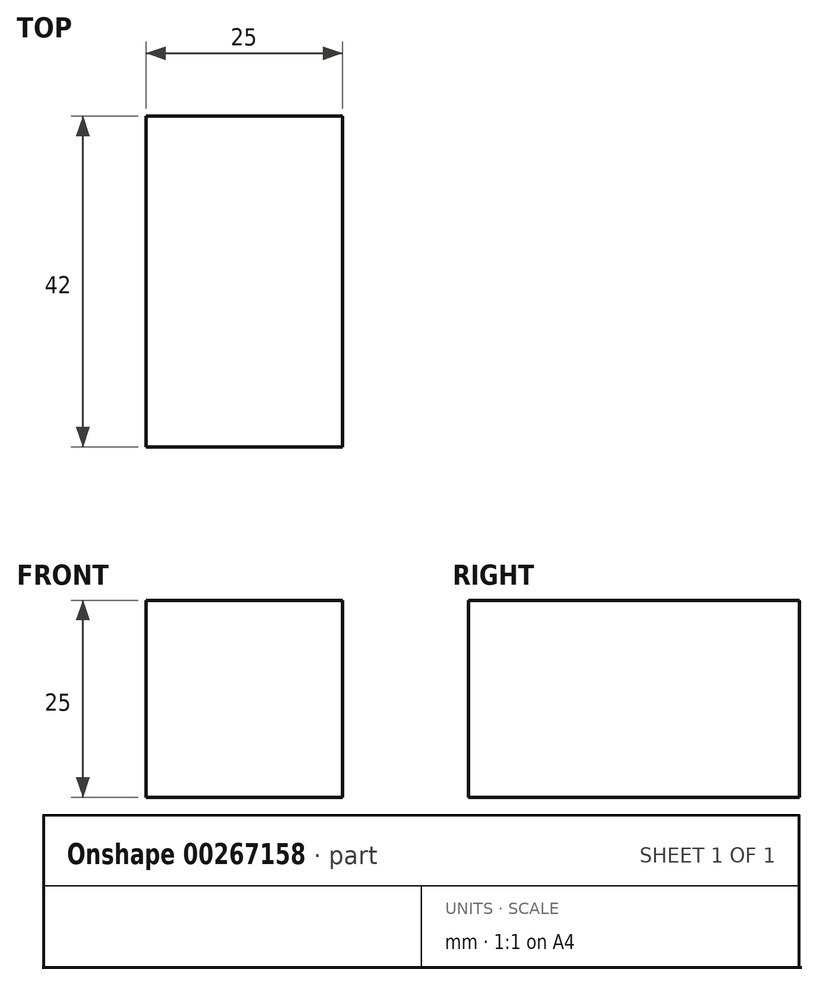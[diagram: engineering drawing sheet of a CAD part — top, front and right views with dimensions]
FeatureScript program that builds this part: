
annotation { "Feature Type Name" : "Feature", "Feature Type Description" : "" }
export const myFeature = defineFeature(function(context is Context, id is Id, definition is map)
    precondition{}
    {
        {
            var Q0;
            Q0=qCreatedBy(makeId("Front.planeOp"),FACE);
            var sketch = newSketch(context, id + "F0", { "sketchPlane" : qUnion([Q0])});
            skLineSegment(sketch, "E0.bottom", {"start": v(0, 0) * mm, "end": v(25, 0) * mm});
            skLineSegment(sketch, "E0.top", {"start": v(0, -25) * mm, "end": v(25, -25) * mm});
            skLineSegment(sketch, "E0.left", {"start": v(0, 0) * mm, "end": v(0, -25) * mm});
            skLineSegment(sketch, "E0.right", {"start": v(25, 0) * mm, "end": v(25, -25) * mm});
            skSolve(sketch);
        }
        {
            var Q0;
            Q0=makeQuery(id+"F0.imprint","IMPRINT",FACE,{"disambiguationData":[TD([[makeQuery(id+"F0.imprint","IMPRINT",EDGE,{"derivedFrom":sQuery(id+"F0.wireOp",EDGE,"E0.bottom")}),-1.0]])]});
            extrude(context, id + "F1", {"entities" : qUnion([Q0]), "depth" : 42 * mm});
        }
    });
